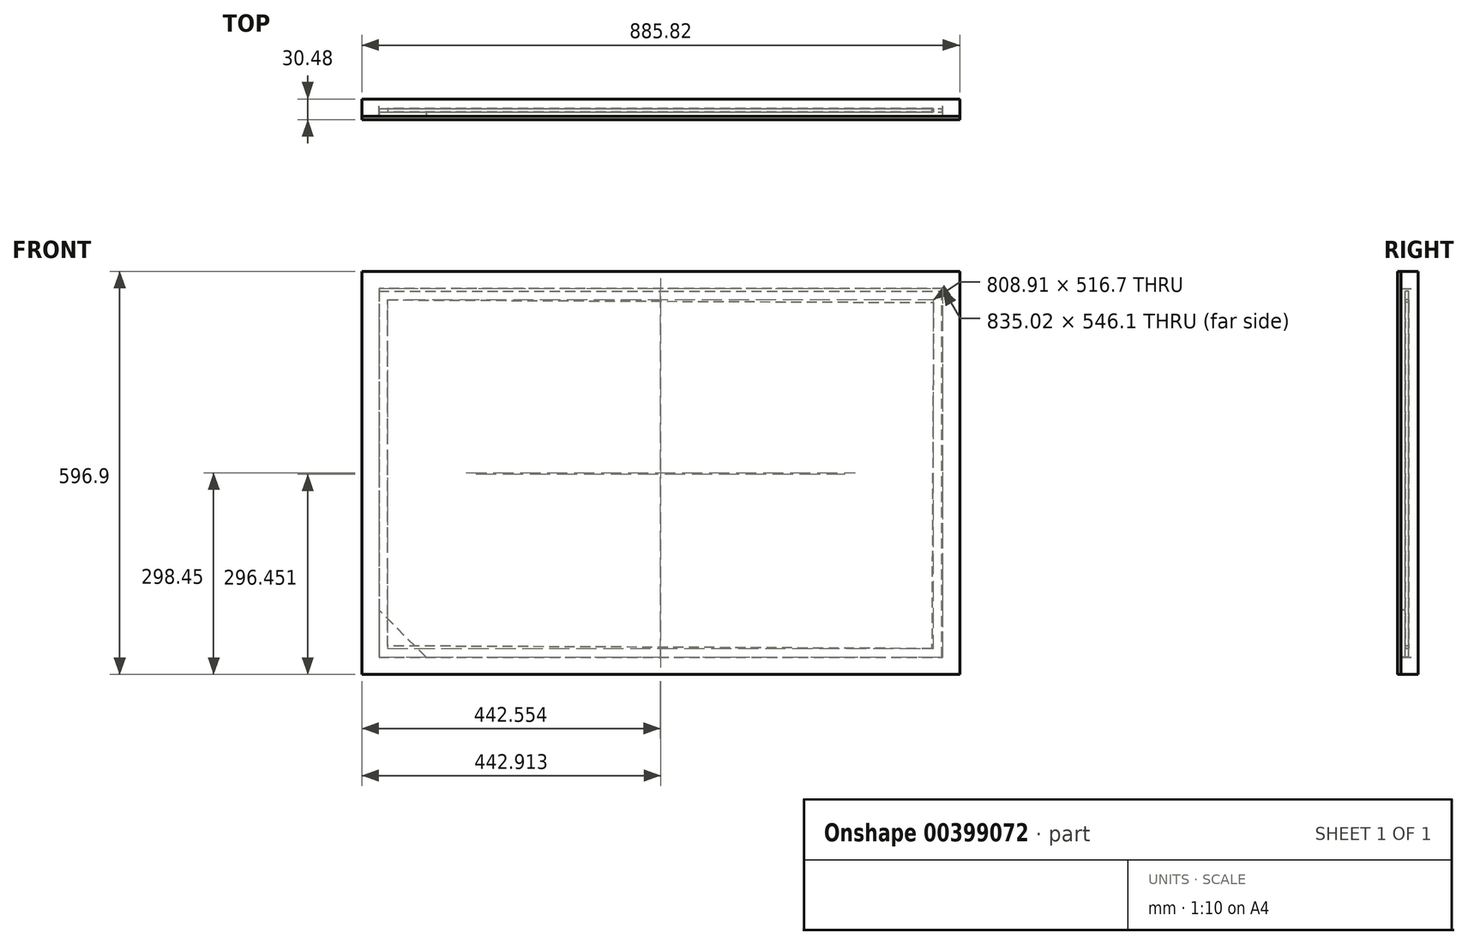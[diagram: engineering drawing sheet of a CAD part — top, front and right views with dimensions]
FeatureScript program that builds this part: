
annotation { "Feature Type Name" : "Feature", "Feature Type Description" : "" }
export const myFeature = defineFeature(function(context is Context, id is Id, definition is map)
    precondition{}
    {
        {
            var Q0;
            Q0=qCreatedBy(makeId("Front.planeOp"),FACE);
            var sketch = newSketch(context, id + "F0", { "sketchPlane" : qUnion([Q0])});
            skLineSegment(sketch, "E0", {"start": v(0, 0) * mm, "end": v(885.83, 0) * mm});
            skLineSegment(sketch, "E1", {"start": v(885.83, 0) * mm, "end": v(885.83, 596.9) * mm});
            skLineSegment(sketch, "E2", {"start": v(885.83, 596.9) * mm, "end": v(0, 596.9) * mm});
            skLineSegment(sketch, "E3", {"start": v(0, 596.9) * mm, "end": v(0, 0) * mm});
            skLineSegment(sketch, "E4", {"start": v(25.4, 571.5) * mm, "end": v(25.4, 25.4) * mm});
            skLineSegment(sketch, "E5", {"start": v(25.4, 25.4) * mm, "end": v(860.43, 25.4) * mm});
            skLineSegment(sketch, "E6", {"start": v(860.43, 25.4) * mm, "end": v(860.43, 571.5) * mm});
            skLineSegment(sketch, "E7", {"start": v(860.43, 571.5) * mm, "end": v(25.4, 571.5) * mm});
            skPoint(sketch, "E8.orphan", {"position": v(25.4, 0) * mm});
            skSolve(sketch);
        }
        {
            var Q0;
            Q0 = qSketchRegion(id + "F0", true);
            extrude(context, id + "F1", {"entities" : qUnion([Q0]), "depth" : 25.4 * mm});
        }
        {
            var Q0;
            Q0=makeQuery(id+"F1.opExtrude","CAP_FACE",FACE,{"disambiguationData":[OSD([sQuery(id+"F0.wireOp",EDGE,"E0"),sQuery(id+"F0.wireOp",EDGE,"E1"),sQuery(id+"F0.wireOp",EDGE,"E2"),sQuery(id+"F0.wireOp",EDGE,"E3"),sQuery(id+"F0.wireOp",EDGE,"E4"),sQuery(id+"F0.wireOp",EDGE,"E5"),sQuery(id+"F0.wireOp",EDGE,"E6"),sQuery(id+"F0.wireOp",EDGE,"E7")])],"isStart":false});
            var sketch = newSketch(context, id + "F2", { "sketchPlane" : qUnion([Q0])});
            skLineSegment(sketch, "E9", {"start": v(25.4, 25.4) * mm, "end": v(25.4, 95.25) * mm});
            skLineSegment(sketch, "E10", {"start": v(25.4, 25.4) * mm, "end": v(95.25, 25.4) * mm});
            skLineSegment(sketch, "E11", {"start": v(95.25, 25.4) * mm, "end": v(25.4, 95.25) * mm});
            skSolve(sketch);
        }
        {
            var Q0;
            Q0 = qSketchRegion(id + "F2", true);
            extrude(context, id + "F3", {"entities" : qUnion([Q0]), "oppositeDirection" : true, "depth" : 6.35 * mm});
        }
        {
            var Q0;
            Q0=makeQuery(id+"F1.opExtrude","CAP_FACE",FACE,{"disambiguationData":[OSD([sQuery(id+"F0.wireOp",EDGE,"E0"),sQuery(id+"F0.wireOp",EDGE,"E1"),sQuery(id+"F0.wireOp",EDGE,"E2"),sQuery(id+"F0.wireOp",EDGE,"E3"),sQuery(id+"F0.wireOp",EDGE,"E4"),sQuery(id+"F0.wireOp",EDGE,"E5"),sQuery(id+"F0.wireOp",EDGE,"E6"),sQuery(id+"F0.wireOp",EDGE,"E7")])],"isStart":false});
            var sketch = newSketch(context, id + "F4", { "sketchPlane" : qUnion([Q0])});
            skLineSegment(sketch, "E12.bottom", {"start": v(0, 596.9) * mm, "end": v(885.83, 596.9) * mm});
            skLineSegment(sketch, "E12.top", {"start": v(0, 0) * mm, "end": v(885.83, 0) * mm});
            skLineSegment(sketch, "E12.left", {"start": v(0, 596.9) * mm, "end": v(0, 0) * mm});
            skLineSegment(sketch, "E12.right", {"start": v(885.83, 596.9) * mm, "end": v(885.83, 0) * mm});
            skSolve(sketch);
        }
        {
            var Q0;
            Q0 = qSketchRegion(id + "F4", true);
            extrude(context, id + "F5", {"entities" : qUnion([Q0]), "depth" : 5.08 * mm});
        }
        {
            var Q0;
            Q0=makeQuery(id+"F3.opExtrude","CAP_FACE",FACE,{"disambiguationData":[OSD([sQuery(id+"F2.wireOp",EDGE,"E9"),sQuery(id+"F2.wireOp",EDGE,"E10"),sQuery(id+"F2.wireOp",EDGE,"E11")])],"isStart":false});
            var sketch = newSketch(context, id + "F6", { "sketchPlane" : qUnion([Q0])});
            skLineSegment(sketch, "E13.bottom", {"start": v(-25.4, 25.4) * mm, "end": v(-859.7, 25.4) * mm});
            skLineSegment(sketch, "E13.top", {"start": v(-25.4, 567.5) * mm, "end": v(-859.7, 567.5) * mm});
            skLineSegment(sketch, "E13.left", {"start": v(-25.4, 25.4) * mm, "end": v(-25.4, 567.5) * mm});
            skLineSegment(sketch, "E13.right", {"start": v(-859.7, 25.4) * mm, "end": v(-859.7, 567.5) * mm});
            skLineSegment(sketch, "E14", {"start": v(-25.4, 25.4) * mm, "end": v(-38.1, 25.4) * mm});
            skLineSegment(sketch, "E15", {"start": v(-38.1, 42.03) * mm, "end": v(-38.1, 554.8) * mm});
            skLineSegment(sketch, "E16", {"start": v(-38.1, 554.8) * mm, "end": v(-847, 550.86) * mm});
            skLineSegment(sketch, "E17", {"start": v(-847, 550.86) * mm, "end": v(-844.51, 38.1) * mm});
            skLineSegment(sketch, "E18", {"start": v(-844.51, 38.1) * mm, "end": v(-38.1, 42.03) * mm});
            skPoint(sketch, "E19.orphan", {"position": v(-844.45, 25.4) * mm});
            skSolve(sketch);
        }
        {
            var Q0;
            Q0 = qSketchRegion(id + "F6", true);
            extrude(context, id + "F7", {"entities" : qUnion([Q0]), "depth" : 5.08 * mm});
        }
    });
